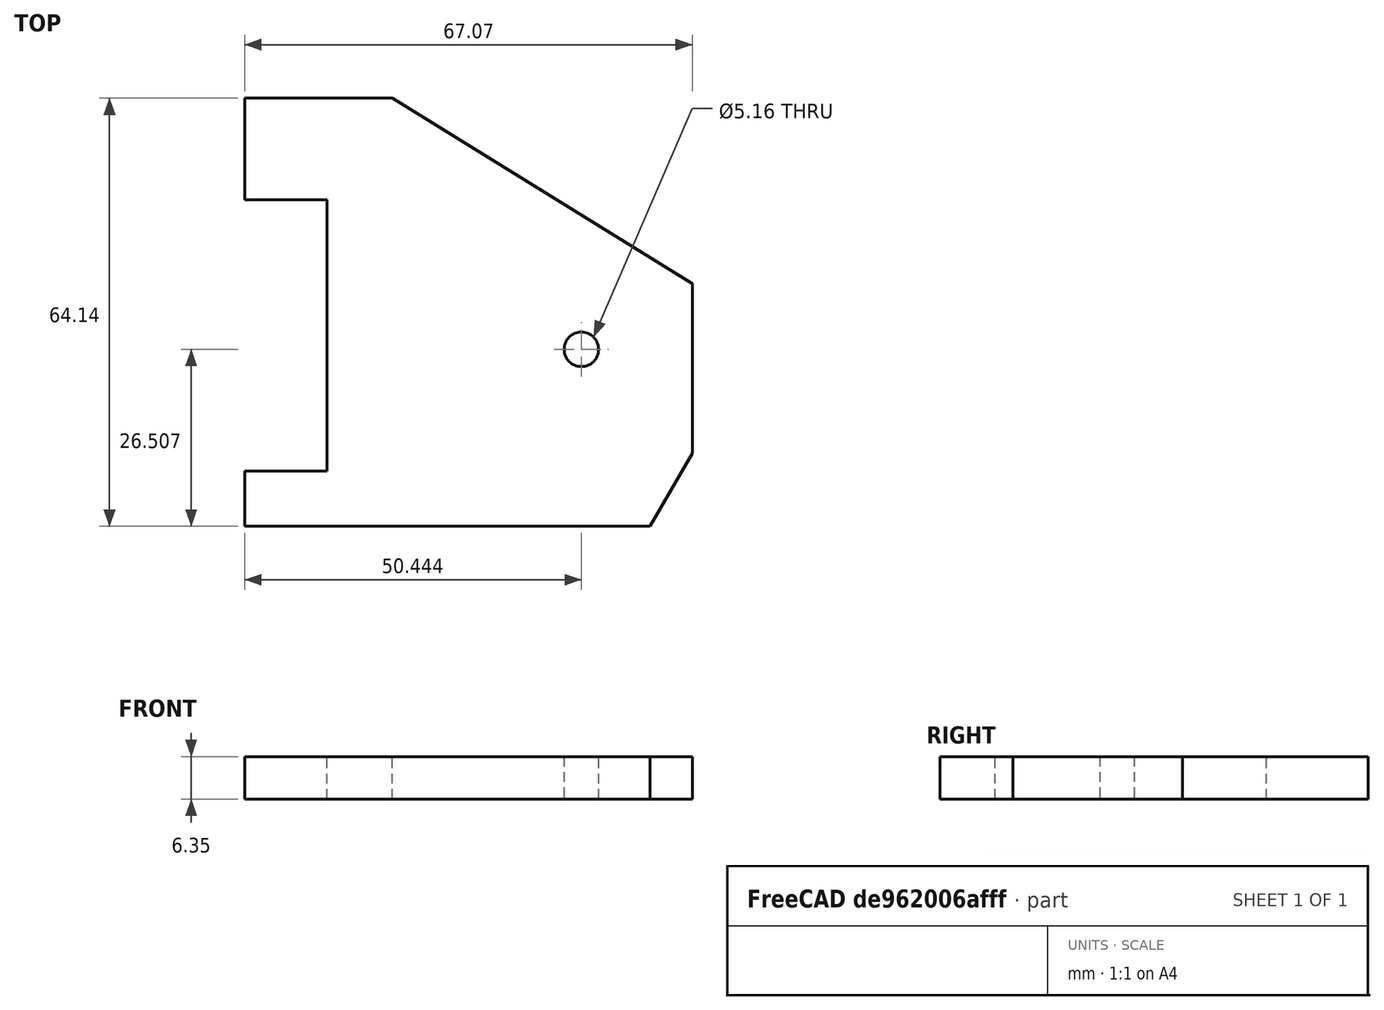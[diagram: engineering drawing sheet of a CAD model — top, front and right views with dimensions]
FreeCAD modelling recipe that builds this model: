
FCSTD DOCUMENT  (FreeCAD 0.19R23964 (Git))
Label: fuse box bracket
License: Creative Commons Attribution-ShareAlike
LicenseURL: http://creativecommons.org/licenses/by-sa/4.0/
objects: Sketcher::SketchObject×1, PartDesign::Pad×1, PartDesign::Body×1
note: 4 computed .brp shape members not serialized (recipe doc carries the construction recipe); baked Part::Feature solids carry a one-line shape summary decoded from their .brp

FEATURE [Sketcher::SketchObject] Sketch
  FullyConstrained = true
  MapMode = 5
  Support = -> [XY_Plane]
  sketch-geometry (11):
    g0: LineSegment StartX=0 StartY=0 StartZ=0 EndX=60.7187 EndY=0 EndZ=0
    g1: LineSegment StartX=60.7187 StartY=0 StartZ=0 EndX=67.0687 EndY=10.922 EndZ=0
    g2: LineSegment StartX=67.0687 StartY=10.922 StartZ=0 EndX=67.0687 EndY=36.322 EndZ=0
    g3: LineSegment StartX=67.0687 StartY=36.322 StartZ=0 EndX=22.098 EndY=64.135 EndZ=0
    g4: LineSegment StartX=22.098 StartY=64.135 StartZ=0 EndX=0 EndY=64.135 EndZ=0
    g5: LineSegment StartX=0 StartY=64.135 StartZ=0 EndX=0 EndY=48.895 EndZ=0
    g6: LineSegment StartX=0 StartY=48.895 StartZ=0 EndX=12.3444 EndY=48.895 EndZ=0
    g7: LineSegment StartX=12.3444 StartY=48.895 StartZ=0 EndX=12.3444 EndY=8.255 EndZ=0
    g8: LineSegment StartX=12.3444 StartY=8.255 StartZ=0 EndX=0 EndY=8.255 EndZ=0
    g9: LineSegment StartX=0 StartY=8.255 StartZ=0 EndX=0 EndY=0 EndZ=0
    g10: Circle CenterX=50.4444 CenterY=26.5074 CenterZ=0 NormalX=0 NormalY=0 NormalZ=1 AngleXU=0 Radius=2.5781
  constraints (32):
    c: Coincident(g0,g-1)
    c: PointOnObject(g0,g-1)
    c: Coincident(g1,g0)
    c: Coincident(g2,g1)
    c: Vertical(g2)
    c: Coincident(g3,g2)
    c: Coincident(g4,g3)
    c: PointOnObject(g4,g-2)
    c: Horizontal(g4)
    c: Coincident(g5,g4)
    c: PointOnObject(g5,g-2)
    c: Coincident(g6,g5)
    c: Horizontal(g6)
    c: Coincident(g7,g6)
    c: Vertical(g7)
    c: Coincident(g8,g7)
    c: PointOnObject(g8,g-2)
    c: Horizontal(g8)
    c: Coincident(g9,g8)
    c: Coincident(g9,g0)
    c: DistanceY(g7,g7) = 40.64
    c: DistanceX(g0,g10) = 50.4444
    c: DistanceY(g0,g1) = 10.922
    c: DistanceY(g1,g2) = 25.4
    c: DistanceY(g0,g10) = 26.5074
    c: DistanceY(g5,g5) = 15.24
    c: DistanceY(g9,g9) = 8.255
    c: DistanceX(g8,g8) = 12.3444
    c: Diameter(g10) = 5.1562
    c: DistanceX(g4,g4) = 22.098
    c: DistanceX(g0,g1) = 6.35
    c: DistanceX(g0,g2) = 67.0687
FEATURE [PartDesign::Pad] Pad
  Direction = (1,1,1)
  Length = 6.35
  Length2 = 99.9998
  Profile = -> Sketch
  Type = 0
FEATURE [PartDesign::Body] Body
  Group = -> [Sketch,Pad]
  Origin = -> Origin
  Tip = -> Pad
